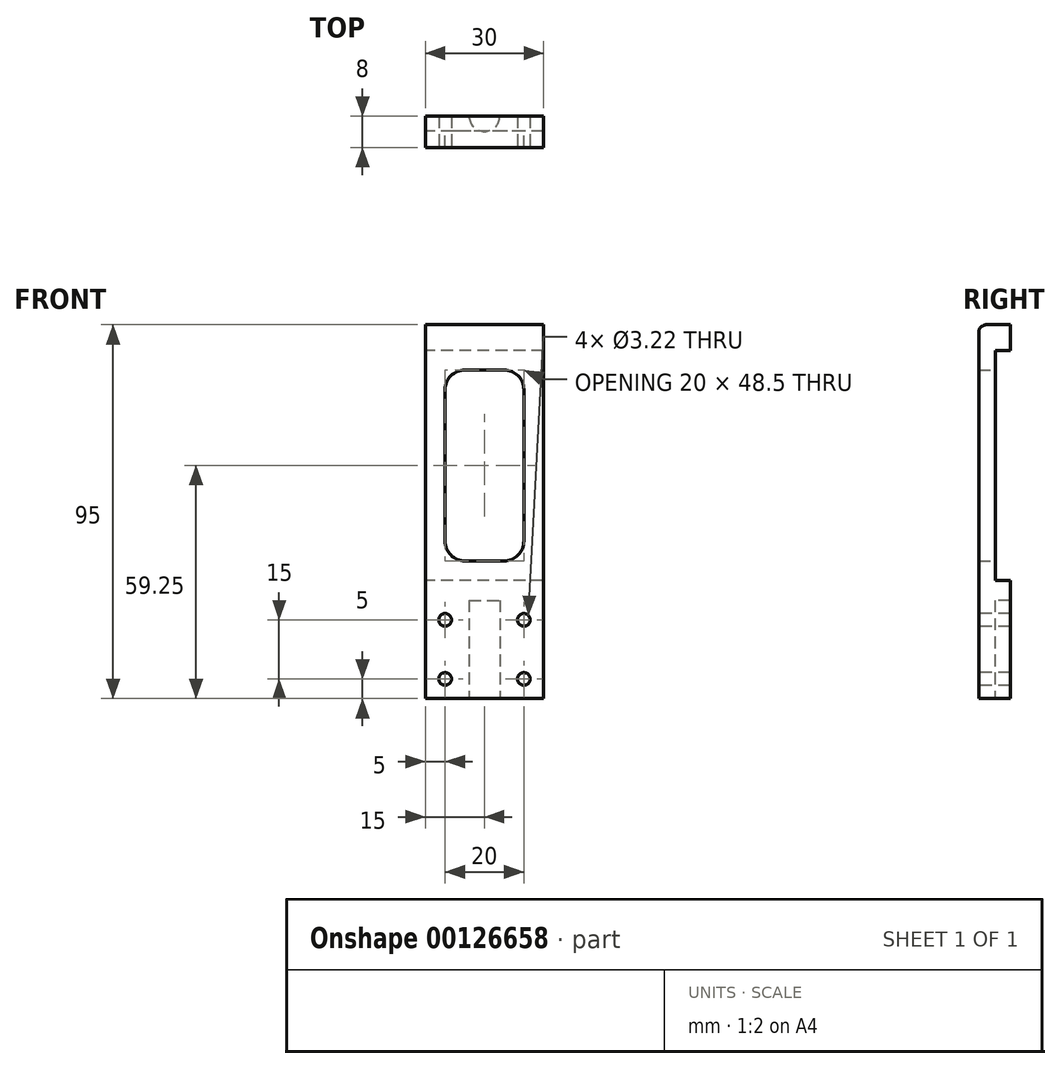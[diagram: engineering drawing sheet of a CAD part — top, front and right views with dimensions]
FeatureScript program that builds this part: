
annotation { "Feature Type Name" : "Feature", "Feature Type Description" : "" }
export const myFeature = defineFeature(function(context is Context, id is Id, definition is map)
    precondition{}
    {
        {
            var Q0;
            Q0=qCreatedBy(makeId("Top.planeOp"),FACE);
            var sketch = newSketch(context, id + "F0", { "sketchPlane" : qUnion([Q0])});
            skLineSegment(sketch, "E0.bottom", {"start": v(-15, 4) * mm, "end": v(15, 4) * mm});
            skLineSegment(sketch, "E0.top", {"start": v(-15, -4) * mm, "end": v(15, -4) * mm});
            skLineSegment(sketch, "E0.left", {"start": v(-15, 4) * mm, "end": v(-15, -4) * mm});
            skLineSegment(sketch, "E0.right", {"start": v(15, 4) * mm, "end": v(15, -4) * mm});
            skLineSegment(sketch, "E1", {"start": v(0, 4) * mm, "end": v(0, -4) * mm, "construction": true});
            skCircle(sketch, "E2", {"center": v(0, 4) * mm, "radius": 3.9 * mm});
            skSolve(sketch);
        }
        {
            var Q0;
            Q0=makeQuery(id+"F0.imprint","IMPRINT",FACE,{"disambiguationData":[TD([[makeQuery(id+"F0.imprint","IMPRINT",EDGE,{"derivedFrom":sQuery(id+"F0.wireOp",EDGE,"E0.top")}),1.0]])]});
            extrude(context, id + "F1", {"entities" : qUnion([Q0]), "depth" : 25 * mm});
        }
        {
            var Q0;
            Q0=makeQuery(id+"F1.opExtrude","SWEPT_FACE",FACE,{"disambiguationData":[OSD([sQuery(id+"F0.wireOp",EDGE,"E0.top")])]});
            var sketch = newSketch(context, id + "F2", { "sketchPlane" : qUnion([Q0])});
            skCircle(sketch, "E3", {"center": v(-10, 5) * mm, "radius": 1.61 * mm});
            skCircle(sketch, "E4.0.1.0", {"center": v(-10, 20) * mm, "radius": 1.61 * mm});
            skCircle(sketch, "E4.1.0.0", {"center": v(10, 5) * mm, "radius": 1.61 * mm});
            skCircle(sketch, "E4.1.1.0", {"center": v(10, 20) * mm, "radius": 1.61 * mm});
            skLineSegment(sketch, "E4.direction1", {"start": v(-10, 5) * mm, "end": v(10, 5) * mm, "construction": true});
            skLineSegment(sketch, "E4.direction2", {"start": v(-10, 5) * mm, "end": v(-10, 20) * mm, "construction": true});
            skSolve(sketch);
        }
        {
            var Q0;
            Q0=makeQuery(id+"F2.imprint","IMPRINT",FACE,{"disambiguationData":[TD([[makeQuery(id+"F2.imprint","IMPRINT",EDGE,{"derivedFrom":sQuery(id+"F2.wireOp",EDGE,"E4.0.1.0")}),1.0]])]});
            var Q1;
            Q1=makeQuery(id+"F2.imprint","IMPRINT",FACE,{"disambiguationData":[TD([[makeQuery(id+"F2.imprint","IMPRINT",EDGE,{"derivedFrom":sQuery(id+"F2.wireOp",EDGE,"E3")}),1.0]])]});
            var Q2;
            Q2=makeQuery(id+"F2.imprint","IMPRINT",FACE,{"disambiguationData":[TD([[makeQuery(id+"F2.imprint","IMPRINT",EDGE,{"derivedFrom":sQuery(id+"F2.wireOp",EDGE,"E4.1.1.0")}),1.0]])]});
            var Q3;
            Q3=makeQuery(id+"F2.imprint","IMPRINT",FACE,{"disambiguationData":[TD([[makeQuery(id+"F2.imprint","IMPRINT",EDGE,{"derivedFrom":sQuery(id+"F2.wireOp",EDGE,"E4.1.0.0")}),1.0]])]});
            extrude(context, id + "F3", {"entities" : qUnion([Q0, Q1, Q2, Q3]), "operationType" : NewBodyOperationType.REMOVE, "oppositeDirection" : true, "depth" : 25 * mm});
        }
        {
            var Q0;
            Q0=makeQuery(id+"F1.opExtrude","CAP_FACE",FACE,{"disambiguationData":[OSD([sQuery(id+"F0.wireOp",EDGE,"E0.bottom"),sQuery(id+"F0.wireOp",EDGE,"E0.top"),sQuery(id+"F0.wireOp",EDGE,"E0.left"),sQuery(id+"F0.wireOp",EDGE,"E0.right"),sQuery(id+"F0.wireOp",EDGE,"E2")])],"isStart":false});
            var sketch = newSketch(context, id + "F4", { "sketchPlane" : qUnion([Q0])});
            skLineSegment(sketch, "E5.bottom", {"start": v(-15, -4) * mm, "end": v(15, -4) * mm});
            skLineSegment(sketch, "E5.top", {"start": v(-15, 4) * mm, "end": v(15, 4) * mm});
            skLineSegment(sketch, "E5.left", {"start": v(-15, -4) * mm, "end": v(-15, 4) * mm});
            skLineSegment(sketch, "E5.right", {"start": v(15, -4) * mm, "end": v(15, 4) * mm});
            skSolve(sketch);
        }
        {
            var Q0;
            Q0=makeQuery(id+"F4.imprint","IMPRINT",FACE,{"disambiguationData":[TD([[makeQuery(id+"F4.imprint","IMPRINT",EDGE,{"derivedFrom":sQuery(id+"F4.wireOp",EDGE,"E5.bottom")}),1.0]])]});
            var Q1;
            {var subQ1=makeQuery(id+"F1.opExtrude","CAP_EDGE",EDGE,{"disambiguationData":[OSD([sQuery(id+"F0.wireOp",EDGE,"E2")])],"isStart":false});Q1=makeQuery(id+"F4.imprint","IMPRINT",FACE,{"disambiguationData":[TD([[makeQuery(id+"F4.imprint","IMPRINT",EDGE,{"derivedFrom":subQ1}),1.0]])]});}
            extrude(context, id + "F5", {"entities" : qUnion([Q0, Q1]), "operationType" : NewBodyOperationType.ADD, "depth" : 70 * mm});
        }
        {
            var Q0;
            Q0=makeQuery(id+"F5.boolean.opBoolean","MERGE",FACE,{"derivedFrom":[makeQuery(id+"F1.opExtrude","SWEPT_FACE",FACE,{"disambiguationData":[OSD([sQuery(id+"F0.wireOp",EDGE,"E0.left")])]}),makeQuery(id+"F5.opExtrude","SWEPT_FACE",FACE,{"disambiguationData":[OSD([sQuery(id+"F4.wireOp",EDGE,"E5.left")])]})]});
            var sketch = newSketch(context, id + "F6", { "sketchPlane" : qUnion([Q0])});
            skLineSegment(sketch, "E6.bottom", {"start": v(-4, 30) * mm, "end": v(-0.25, 30) * mm});
            skLineSegment(sketch, "E6.top", {"start": v(-4, 88.5) * mm, "end": v(-0.25, 88.5) * mm});
            skLineSegment(sketch, "E6.left", {"start": v(-4, 30) * mm, "end": v(-4, 88.5) * mm});
            skLineSegment(sketch, "E6.right", {"start": v(-0.25, 30) * mm, "end": v(-0.25, 88.5) * mm});
            skSolve(sketch);
        }
        {
            var Q0;
            Q0=makeQuery(id+"F6.imprint","IMPRINT",FACE,{"disambiguationData":[TD([[makeQuery(id+"F6.imprint","IMPRINT",EDGE,{"derivedFrom":sQuery(id+"F6.wireOp",EDGE,"E6.bottom")}),1.0]])]});
            extrude(context, id + "F7", {"entities" : qUnion([Q0]), "operationType" : NewBodyOperationType.REMOVE, "endBound" : BoundingType.THROUGH_ALL, "oppositeDirection" : true, "depth" : 25 * mm});
        }
        {
            var Q0;
            Q0=makeQuery(id+"F7.boolean.opBoolean","COPY",FACE,{"derivedFrom":makeQuery(id+"F7.opExtrude","SWEPT_FACE",FACE,{"disambiguationData":[OSD([sQuery(id+"F6.wireOp",EDGE,"E6.right")])]})});
            var sketch = newSketch(context, id + "F8", { "sketchPlane" : qUnion([Q0])});
            skLineSegment(sketch, "E7.bottom", {"start": v(-10, 83.5) * mm, "end": v(10, 83.5) * mm});
            skLineSegment(sketch, "E7.top", {"start": v(-10, 35) * mm, "end": v(10, 35) * mm});
            skLineSegment(sketch, "E7.left", {"start": v(-10, 83.5) * mm, "end": v(-10, 35) * mm});
            skLineSegment(sketch, "E7.right", {"start": v(10, 83.5) * mm, "end": v(10, 35) * mm});
            skSolve(sketch);
        }
        {
            var Q0;
            Q0=makeQuery(id+"F8.imprint","IMPRINT",FACE,{"disambiguationData":[TD([[makeQuery(id+"F8.imprint","IMPRINT",EDGE,{"derivedFrom":sQuery(id+"F8.wireOp",EDGE,"E7.bottom")}),-1.0]])]});
            extrude(context, id + "F9", {"entities" : qUnion([Q0]), "operationType" : NewBodyOperationType.REMOVE, "oppositeDirection" : true, "depth" : 25 * mm});
        }
        {
            var Q0;
            Q0=makeQuery(id+"F9.boolean.opBoolean","COPY",EDGE,{"derivedFrom":makeQuery(id+"F9.opExtrude","SWEPT_EDGE",EDGE,{"disambiguationData":[OSD([sQuery(id+"F8.wireOp",EDGE,"E7.top"),sQuery(id+"F8.wireOp",EDGE,"E7.left")])]})});
            var Q1;
            Q1=makeQuery(id+"F9.boolean.opBoolean","COPY",EDGE,{"derivedFrom":makeQuery(id+"F9.opExtrude","SWEPT_EDGE",EDGE,{"disambiguationData":[OSD([sQuery(id+"F8.wireOp",EDGE,"E7.bottom"),sQuery(id+"F8.wireOp",EDGE,"E7.right")])]})});
            var Q2;
            Q2=makeQuery(id+"F9.boolean.opBoolean","COPY",EDGE,{"derivedFrom":makeQuery(id+"F9.opExtrude","SWEPT_EDGE",EDGE,{"disambiguationData":[OSD([sQuery(id+"F8.wireOp",EDGE,"E7.top"),sQuery(id+"F8.wireOp",EDGE,"E7.right")])]})});
            var Q3;
            Q3=makeQuery(id+"F9.boolean.opBoolean","COPY",EDGE,{"derivedFrom":makeQuery(id+"F9.opExtrude","SWEPT_EDGE",EDGE,{"disambiguationData":[OSD([sQuery(id+"F8.wireOp",EDGE,"E7.bottom"),sQuery(id+"F8.wireOp",EDGE,"E7.left")])]})});
            fillet(context, id + "F10", {"entities" : qUnion([Q0, Q1, Q2, Q3]), "radius" : 5 * mm, "tangentPropagation" : true, "allowEdgeOverflow" : false});
        }
        {
            var Q0;
            Q0=makeQuery(id+"F5.opExtrude","CAP_EDGE",EDGE,{"disambiguationData":[OSD([sQuery(id+"F4.wireOp",EDGE,"E5.bottom")])],"isStart":false});
            fillet(context, id + "F11", {"entities" : qUnion([Q0]), "radius" : 2 * mm, "tangentPropagation" : true, "allowEdgeOverflow" : false});
        }
    });
